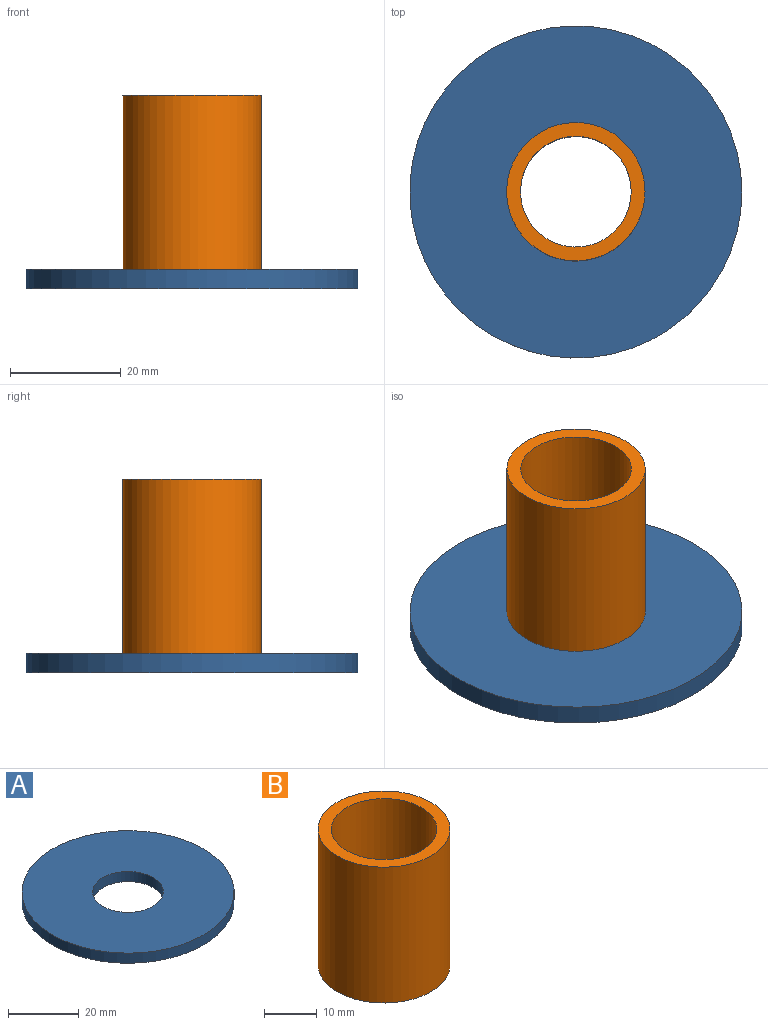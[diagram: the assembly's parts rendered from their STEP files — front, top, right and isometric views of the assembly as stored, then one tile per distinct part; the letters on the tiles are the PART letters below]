
ASSEMBLY  parts=2 mates=1
PART A: 4 faces, bbox 60x60x3.5 mm
  f0: cylinder r=10mm len=20mm, axis (0,0,-1), area 219.9mm2, adj f2,f3
  f1: cylinder r=30mm len=60mm, axis (0,0,-1), area 659.7mm2, adj f2,f3
  f2: plane 60x60mm, normal (0,0,1), area 2513.3mm2, adj f0,f1
  f3: plane 60x60mm, normal (0,0,-1), area 2513.3mm2, adj f0,f1
PART B: 4 faces, bbox 25x25x31.5 mm
  f0: cylinder r=10mm len=31.5mm, axis (0,0,-1), area 1979.2mm2, adj f2,f3
  f1: cylinder r=12.5mm len=31.5mm, axis (0,0,-1), area 2474mm2, adj f2,f3
  f2: plane 25x25mm, normal (0,0,1), area 176.7mm2, adj f0,f1
  f3: plane 25x25mm, normal (0,0,-1), area 176.7mm2, adj f0,f1
PLACE A t=(-62.57,15.97,21.91)mm
PLACE B rot(axis=(1,0,0),180deg) t=(54,-23.68,56.91)mm
MATE fastened B.f0 <-> A.f0  axis (0,0,1) through (-40.61,-7.34,25.41)mm
